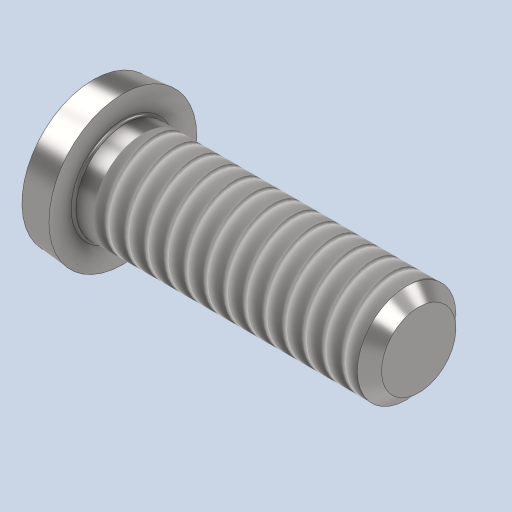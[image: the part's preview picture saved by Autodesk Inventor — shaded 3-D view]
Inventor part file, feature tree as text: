
AUTODESK INVENTOR PART (.ipt)
format: ipt  version: 2023 (Build 270158000, 158)  size: 245,248 bytes
history: native  units: mm
features: other x7, sketch x4, revolve x3, thread x1, extrude x1
ambient origin geometry x8: Origin, YZ Plane, XZ Plane, XY Plane, X Axis, Y Axis, Z Axis, Center Point
bodies: Solid1 (feature_tree)
feature tree (16):
  revolve  "Revolution1"  [1 undecoded]
  thread  "Thread1"  [1 undecoded]
  revolve  "Revolution2"  Angle=360.0deg
  extrude  "Extrusion1"  [1 undecoded]
  revolve  "Revolution3"  [1 undecoded]
  other  "screw_to_rail_XY"
  other  "screw_to_rail_YZ"
  other  "screw_to_rail_ZX"
  other  "screw_to_rail_X"
  other  "screw_to_rail_Y"
  other  "screw_to_rail_Z"
  other  "screw_to_rail_Center"
  sketch  "Sketch_1"  dims[d0=360.0deg d1=5.3545mm d2=0.0mm d3=360.0deg]
  sketch  "Sketch_3"  dims[d4=0.3mm d5=0.0mm d6=360.0deg]
  sketch  "Sketch_5"  dims[d7=0.0mm]
  sketch  "Sketch_6"
note: 4 required parameter values undecoded (feature->parameter linkage not recoverable at this tier; creation-order binding heuristic only, values carry confidence <= 0.55)